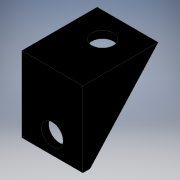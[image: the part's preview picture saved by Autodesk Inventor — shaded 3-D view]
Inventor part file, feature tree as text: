
AUTODESK INVENTOR PART (.ipt)
format: ipt  version: 2018.3 (Build 223284000, 284)  size: 134,144 bytes
history: native  units: mm
features: extrude x6, sketch x6, other x1
ambient origin geometry x8: Origin, YZ Plane, XZ Plane, XY Plane, X Axis, Y Axis, Z Axis, Center Point
bodies: Body1 (feature_tree)
feature tree (13):
  other  "Sólido1"
  extrude  "Extrusión1"  Depth=21.0mm
  extrude  "Extrusión3"  Depth=2.0mm TaperAngle=0.0deg
  extrude  "Extrusión5"  Depth=19.0mm TaperAngle=0.0deg
  extrude  "Extrusión6"  Depth=19.0mm TaperAngle=0.0deg
  extrude  "Extrusión7"  Depth=19.0mm TaperAngle=0.0deg
  extrude  "Extrusión8"  [1 undecoded]
  sketch  "Boceto2"  dims[d0=17.0mm d1=21.0mm]
  sketch  "Boceto3"  dims[d2=17.0mm d3=2.0mm d4=0.0mm]
  sketch  "Boceto5"  dims[d5=21.0mm d8=19.0mm d9=0.0mm]
  sketch  "Boceto6"  dims[d16=19.0mm d17=0.0mm d19=19.0mm d20=0.0mm]
  sketch  "Boceto7"  dims[d24=19.0mm d25=0.0mm d29=19.0mm d30=0.0mm]
  sketch  "Boceto8"
note: 1 required parameter value undecoded (feature->parameter linkage not recoverable at this tier; creation-order binding heuristic only, values carry confidence <= 0.55)
